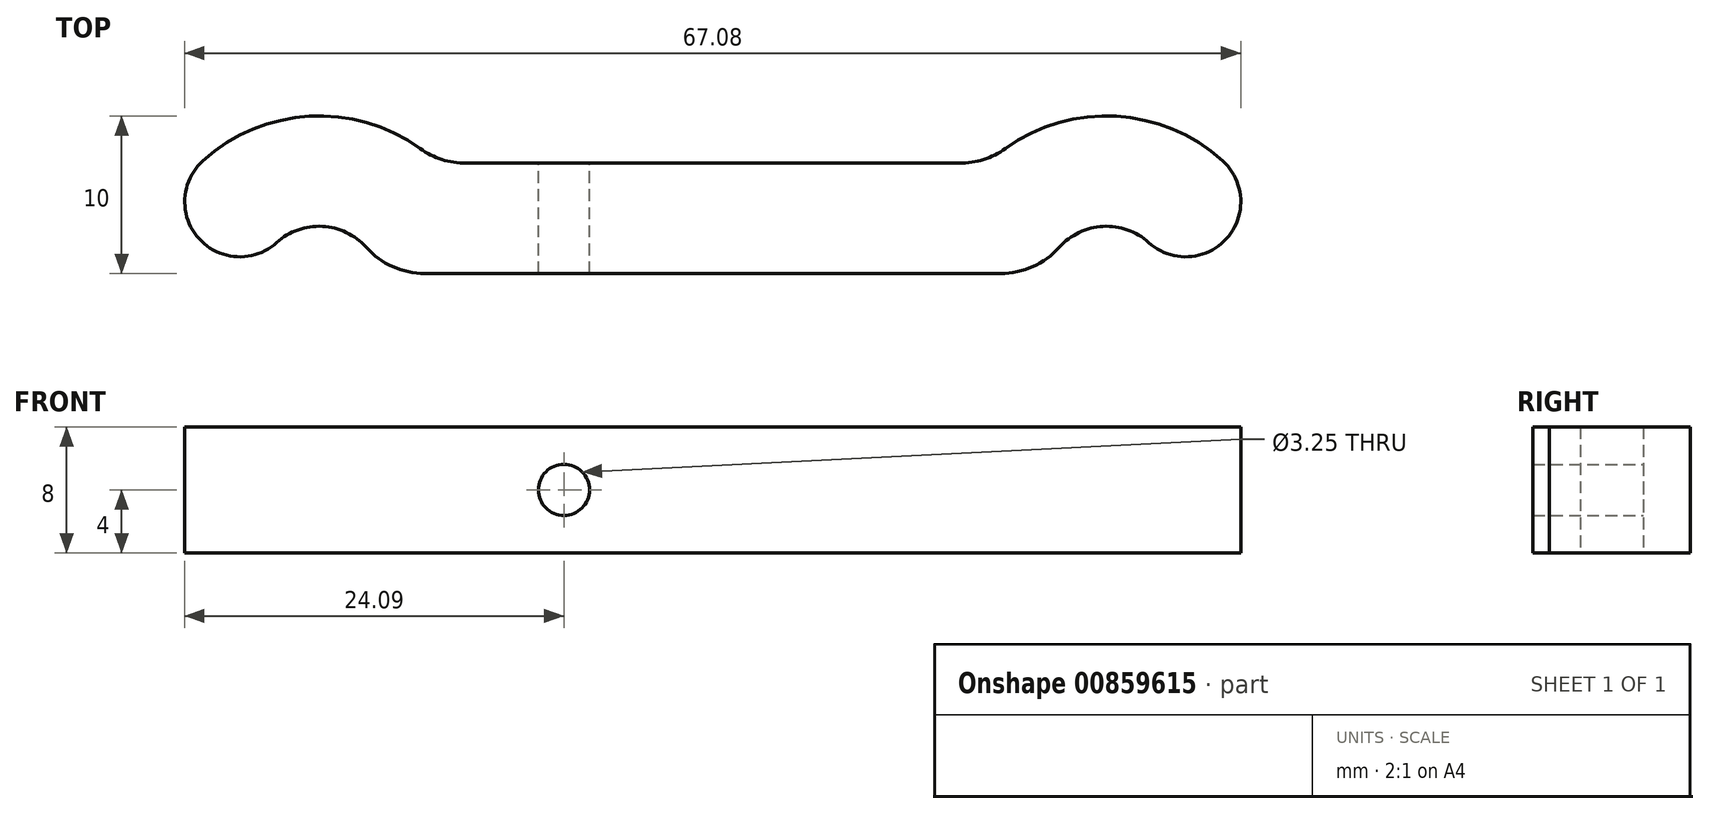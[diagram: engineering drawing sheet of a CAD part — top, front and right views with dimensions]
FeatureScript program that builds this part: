
annotation { "Feature Type Name" : "Feature", "Feature Type Description" : "" }
export const myFeature = defineFeature(function(context is Context, id is Id, definition is map)
    precondition{}
    {
        {
            assignVariable(context, id + "F0", {"name" : "PartThickness", "anyValue" : 7});
        }
        {
            var Q0;
            Q0=qCreatedBy(makeId("Top.planeOp"),FACE);
            var sketch = newSketch(context, id + "F1", { "sketchPlane" : qUnion([Q0])});
            skLineSegment(sketch, "E0", {"start": v(-17.45, 7) * mm, "end": v(0, 7) * mm});
            skArc(sketch, "E1", {"start": v(-17.45, 7) * mm, "mid": v(-27.54, 9.7) * mm, "end": v(-35.34, 2.76) * mm});
            skLineSegment(sketch, "E2", {"start": v(0, 7) * mm, "end": v(0, 0) * mm});
            skLineSegment(sketch, "E3", {"start": v(0, 0) * mm, "end": v(-21.13, 0) * mm});
            skArc(sketch, "E4", {"start": v(-21.13, 0) * mm, "mid": v(-24.8, 3) * mm, "end": v(-28.76, 0.37) * mm});
            skLineSegment(sketch, "E5", {"start": v(-35.34, 2.76) * mm, "end": v(-28.76, 0.37) * mm});
            skLineSegment(sketch, "E6.MirrorCS", {"start": v(0, 0) * mm, "end": v(21.13, 0) * mm, "construction": true});
            skLineSegment(sketch, "E7.MirrorCS", {"start": v(35.34, 2.76) * mm, "end": v(28.76, 0.37) * mm, "construction": true});
            skLineSegment(sketch, "E8.MirrorCS", {"start": v(17.45, 7) * mm, "end": v(0, 7) * mm, "construction": true});
            skArc(sketch, "E9.MirrorCS", {"start": v(21.13, 0) * mm, "mid": v(24.8, 3) * mm, "end": v(28.76, 0.37) * mm, "construction": true});
            skArc(sketch, "E10.MirrorCS", {"start": v(17.45, 7) * mm, "mid": v(27.54, 9.7) * mm, "end": v(35.34, 2.76) * mm, "construction": true});
            skSolve(sketch);
        }
        {
            var Q0;
            Q0 = qSketchRegion(id + "F1", true);
            extrude(context, id + "F2", {"entities" : qUnion([Q0]), "depth" : 8 * mm, "offsetDistance" : 25 * mm});
        }
        {
            var Q0;
            Q0=makeQuery(id+"F2.opExtrude","SWEPT_FACE",FACE,{"disambiguationData":[OSD([sQuery(id+"F1.wireOp",EDGE,"E0"),sQuery(id+"F1.wireOp",EDGE,"E8.MirrorCS")])]});
            var sketch = newSketch(context, id + "F3", { "sketchPlane" : qUnion([Q0])});
            skCircle(sketch, "E11", {"center": v(9.45, 4) * mm, "radius": 1.63 * mm});
            skLineSegment(sketch, "E12", {"start": v(9.45, 8) * mm, "end": v(9.45, 0) * mm, "construction": true});
            skSolve(sketch);
        }
        {
            var Q0;
            Q0=makeQuery(id+"F2.opExtrude","SWEPT_EDGE",EDGE,{"disambiguationData":[OSD([sQuery(id+"F1.wireOp",EDGE,"E0"),sQuery(id+"F1.wireOp",EDGE,"E1")])]});
            var Q1;
            Q1=makeQuery(id+"F2.opExtrude","SWEPT_EDGE",EDGE,{"disambiguationData":[OSD([sQuery(id+"F1.wireOp",EDGE,"E3"),sQuery(id+"F1.wireOp",EDGE,"E4")])]});
            fillet(context, id + "F4", {"entities" : qUnion([Q0, Q1]), "radius" : 5 * mm, "tangentPropagation" : true, "allowEdgeOverflow" : false});
        }
        {
            var Q0;
            Q0=makeQuery(id+"F2.opExtrude","SWEPT_EDGE",EDGE,{"disambiguationData":[OSD([sQuery(id+"F1.wireOp",EDGE,"E1"),sQuery(id+"F1.wireOp",EDGE,"E5")])]});
            var Q1;
            Q1=makeQuery(id+"F2.opExtrude","SWEPT_EDGE",EDGE,{"disambiguationData":[OSD([sQuery(id+"F1.wireOp",EDGE,"E4"),sQuery(id+"F1.wireOp",EDGE,"E5")])]});
            fillet(context, id + "F5", {"entities" : qUnion([Q0, Q1]), "radius" : (getVariable(context, 'PartThickness') / 2) * mm, "tangentPropagation" : true, "allowEdgeOverflow" : false});
        }
        {
            var Q0;
            Q0=makeQuery(id+"F1.imprint","IMPRINT",FACE,{"disambiguationData":[TD([[makeQuery(id+"F1.imprint","IMPRINT",EDGE,{"derivedFrom":sQuery(id+"F1.wireOp",EDGE,"E0")}),-1.0]])]});
            var sketch = newSketch(context, id + "F6", { "sketchPlane" : qUnion([Q0])});
            skLineSegment(sketch, "E13", {"start": v(-25, -1) * mm, "end": v(0, -1) * mm, "construction": true});
            skFitSpline(sketch, "E14", {"points": [v(0, -1) * mm, v(-12.5, 0) * mm], "startDerivative": vector(-18.75, 0) * mm, "endDerivative": vector(-15, 0) * mm});
            skLineSegment(sketch, "E15", {"start": v(0, -1) * mm, "end": v(0, 0) * mm});
            skLineSegment(sketch, "E16", {"start": v(0, 0) * mm, "end": v(-12.5, 0) * mm});
            skSolve(sketch);
        }
        {
            var Q0;
            Q0=makeQuery(id+"F2.opExtrude","SWEPT_BODY",BODY,{"disambiguationData":[OSD([sQuery(id+"F1.wireOp",EDGE,"E0"),sQuery(id+"F1.wireOp",EDGE,"E1"),sQuery(id+"F1.wireOp",EDGE,"E2"),sQuery(id+"F1.wireOp",EDGE,"E3"),sQuery(id+"F1.wireOp",EDGE,"E4"),sQuery(id+"F1.wireOp",EDGE,"E5")])]});
            var Q1;
            Q1=makeQuery(id+"F2.opExtrude","SWEPT_FACE",FACE,{"disambiguationData":[OSD([sQuery(id+"F1.wireOp",EDGE,"E2")])]});
            mirror(context, id + "F7", {"operationType" : NewBodyOperationType.ADD, "entities" : qUnion([Q0]), "mirrorPlane" : qUnion([Q1])});
        }
        {
            var Q0;
            Q0 = qSketchRegion(id + "F3", true);
            extrude(context, id + "F8", {"entities" : qUnion([Q0]), "operationType" : NewBodyOperationType.REMOVE, "endBound" : BoundingType.THROUGH_ALL, "oppositeDirection" : true, "depth" : 25 * mm, "offsetDistance" : 25 * mm});
        }
    });
